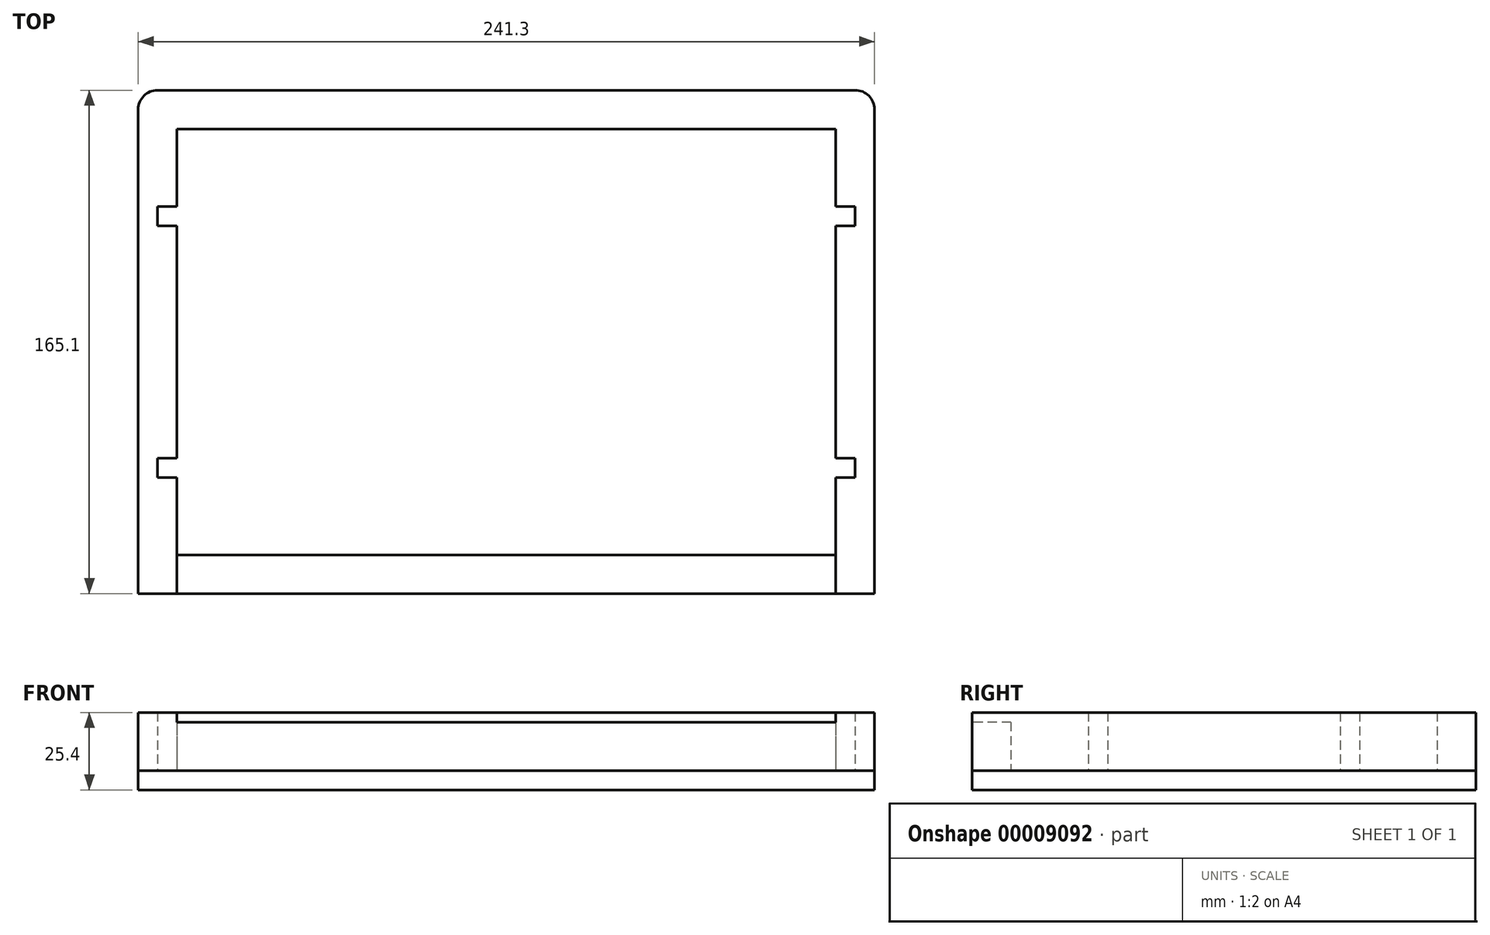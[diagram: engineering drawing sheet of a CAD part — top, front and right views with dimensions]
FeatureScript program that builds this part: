
annotation { "Feature Type Name" : "Feature", "Feature Type Description" : "" }
export const myFeature = defineFeature(function(context is Context, id is Id, definition is map)
    precondition{}
    {
        {
            var Q0;
            Q0=qCreatedBy(makeId("Top.planeOp"),FACE);
            var sketch = newSketch(context, id + "F0", { "sketchPlane" : qUnion([Q0])});
            skLineSegment(sketch, "E0.rect.bottom", {"start": v(107.95, 69.85) * mm, "end": v(-107.95, 69.85) * mm});
            skLineSegment(sketch, "E0.rect.top", {"start": v(107.95, -69.85) * mm, "end": v(-107.95, -69.85) * mm});
            skLineSegment(sketch, "E0.rect.left", {"start": v(107.95, 69.85) * mm, "end": v(107.95, 44.45) * mm});
            skLineSegment(sketch, "E0.rect.right", {"start": v(-107.95, 69.85) * mm, "end": v(-107.95, 44.45) * mm});
            skPoint(sketch, "E0.rect.middle", {"position": v(0, 0) * mm});
            skLineSegment(sketch, "E1.rect.bottom", {"start": v(120.65, 82.55) * mm, "end": v(-120.65, 82.55) * mm});
            skLineSegment(sketch, "E1.rect.top", {"start": v(120.65, -82.55) * mm, "end": v(-120.65, -82.55) * mm});
            skLineSegment(sketch, "E1.rect.left", {"start": v(120.65, 82.55) * mm, "end": v(120.65, -82.55) * mm});
            skLineSegment(sketch, "E1.rect.right", {"start": v(-120.65, 82.55) * mm, "end": v(-120.65, -82.55) * mm});
            skLineSegment(sketch, "E2.bottom", {"start": v(-107.95, 38.1) * mm, "end": v(-114.3, 38.1) * mm});
            skLineSegment(sketch, "E2.top", {"start": v(-107.95, 44.45) * mm, "end": v(-114.3, 44.45) * mm});
            skLineSegment(sketch, "E2.right", {"start": v(-114.3, 44.45) * mm, "end": v(-114.3, 38.1) * mm});
            skLineSegment(sketch, "E3.bottom", {"start": v(-107.95, -38.1) * mm, "end": v(-114.3, -38.1) * mm});
            skLineSegment(sketch, "E3.top", {"start": v(-107.95, -44.45) * mm, "end": v(-114.3, -44.45) * mm});
            skLineSegment(sketch, "E3.right", {"start": v(-114.3, -38.1) * mm, "end": v(-114.3, -44.45) * mm});
            skLineSegment(sketch, "E4.trimOffspring", {"start": v(-107.95, 38.1) * mm, "end": v(-107.95, -38.1) * mm});
            skLineSegment(sketch, "E5.trimOffspring", {"start": v(-107.95, -44.45) * mm, "end": v(-107.95, -69.85) * mm});
            skLineSegment(sketch, "E6", {"start": v(0, 82.55) * mm, "end": v(0, -82.55) * mm, "construction": true});
            skLineSegment(sketch, "E7.0.MirrorCS", {"start": v(107.95, 38.1) * mm, "end": v(107.95, -38.1) * mm});
            skLineSegment(sketch, "E7.1.MirrorCS", {"start": v(107.95, 38.1) * mm, "end": v(114.3, 38.1) * mm});
            skLineSegment(sketch, "E7.2.MirrorCS", {"start": v(114.3, 44.45) * mm, "end": v(114.3, 38.1) * mm});
            skLineSegment(sketch, "E7.4.MirrorCS", {"start": v(107.95, 44.45) * mm, "end": v(114.3, 44.45) * mm});
            skLineSegment(sketch, "E8.0.MirrorCS", {"start": v(114.3, -38.1) * mm, "end": v(114.3, -44.45) * mm});
            skLineSegment(sketch, "E8.1.MirrorCS", {"start": v(107.95, -44.45) * mm, "end": v(107.95, -69.85) * mm});
            skLineSegment(sketch, "E8.2.MirrorCS", {"start": v(107.95, -44.45) * mm, "end": v(114.3, -44.45) * mm});
            skLineSegment(sketch, "E8.3.MirrorCS", {"start": v(107.95, -38.1) * mm, "end": v(114.3, -38.1) * mm});
            skSolve(sketch);
        }
        {
            var Q0;
            Q0 = qSketchRegion(id + "F0", true);
            extrude(context, id + "F1", {"entities" : qUnion([Q0]), "depth" : 19.05 * mm});
        }
        {
            var Q0;
            Q0=qCreatedBy(makeId("Top.planeOp"),FACE);
            var sketch = newSketch(context, id + "F2", { "sketchPlane" : qUnion([Q0])});
            skLineSegment(sketch, "E9.rect.bottom", {"start": v(-120.65, -82.55) * mm, "end": v(120.65, -82.55) * mm});
            skLineSegment(sketch, "E9.rect.top", {"start": v(-120.65, 82.55) * mm, "end": v(120.65, 82.55) * mm});
            skLineSegment(sketch, "E9.rect.left", {"start": v(-120.65, -82.55) * mm, "end": v(-120.65, 82.55) * mm});
            skLineSegment(sketch, "E9.rect.right", {"start": v(120.65, -82.55) * mm, "end": v(120.65, 82.55) * mm});
            skPoint(sketch, "E9.rect.middle", {"position": v(0, 0) * mm});
            skSolve(sketch);
        }
        {
            var Q0;
            Q0=makeQuery(id+"F2.imprint","IMPRINT",FACE,{"disambiguationData":[TD([[makeQuery(id+"F2.imprint","IMPRINT",EDGE,{"derivedFrom":sQuery(id+"F2.wireOp",EDGE,"E9.rect.bottom")}),1.0]])]});
            extrude(context, id + "F3", {"entities" : qUnion([Q0]), "oppositeDirection" : true, "depth" : 6.35 * mm});
        }
        {
            var Q0;
            Q0=makeQuery(id+"F1.opExtrude","SWEPT_FACE",FACE,{"disambiguationData":[OSD([sQuery(id+"F0.wireOp",EDGE,"E1.rect.top")])]});
            var sketch = newSketch(context, id + "F4", { "sketchPlane" : qUnion([Q0])});
            skLineSegment(sketch, "E10.bottom", {"start": v(-107.95, 19.05) * mm, "end": v(107.95, 19.05) * mm});
            skLineSegment(sketch, "E10.top", {"start": v(-107.95, 15.88) * mm, "end": v(107.95, 15.88) * mm});
            skLineSegment(sketch, "E10.left", {"start": v(-107.95, 19.05) * mm, "end": v(-107.95, 15.88) * mm});
            skLineSegment(sketch, "E10.right", {"start": v(107.95, 19.05) * mm, "end": v(107.95, 15.88) * mm});
            skLineSegment(sketch, "E11", {"start": v(0, 19.05) * mm, "end": v(0, 0) * mm, "construction": true});
            skSolve(sketch);
        }
        {
            var Q0;
            Q0 = qSketchRegion(id + "F4", true);
            var Q1;
            Q1=makeQuery(id+"F1.opExtrude","SWEPT_FACE",FACE,{"disambiguationData":[OSD([sQuery(id+"F0.wireOp",EDGE,"E0.rect.top")])]});
            extrude(context, id + "F5", {"entities" : qUnion([Q0]), "operationType" : NewBodyOperationType.REMOVE, "endBound" : BoundingType.UP_TO_SURFACE, "oppositeDirection" : true, "endBoundEntityFace" : qUnion([Q1]), "depth" : 25.4 * mm});
        }
        {
            var Q0;
            Q0=makeQuery(id+"F1.opExtrude","SWEPT_EDGE",EDGE,{"disambiguationData":[OSD([sQuery(id+"F0.wireOp",EDGE,"E1.rect.bottom"),sQuery(id+"F0.wireOp",EDGE,"E1.rect.right")])]});
            var Q1;
            Q1=makeQuery(id+"F3.opExtrude","SWEPT_EDGE",EDGE,{"disambiguationData":[OSD([sQuery(id+"F2.wireOp",EDGE,"E9.rect.top"),sQuery(id+"F2.wireOp",EDGE,"E9.rect.left")])]});
            var Q2;
            Q2=makeQuery(id+"F3.opExtrude","SWEPT_EDGE",EDGE,{"disambiguationData":[OSD([sQuery(id+"F2.wireOp",EDGE,"E9.rect.top"),sQuery(id+"F2.wireOp",EDGE,"E9.rect.right")])]});
            var Q3;
            Q3=makeQuery(id+"F1.opExtrude","SWEPT_EDGE",EDGE,{"disambiguationData":[OSD([sQuery(id+"F0.wireOp",EDGE,"E1.rect.bottom"),sQuery(id+"F0.wireOp",EDGE,"E1.rect.left")])]});
            fillet(context, id + "F6", {"entities" : qUnion([Q0, Q1, Q2, Q3]), "radius" : 6.35 * mm, "tangentPropagation" : true, "allowEdgeOverflow" : false});
        }
    });
